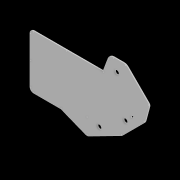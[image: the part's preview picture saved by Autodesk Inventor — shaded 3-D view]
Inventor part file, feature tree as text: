
AUTODESK INVENTOR PART (.ipt)
format: ipt  version: 2020 (Build 240168000, 168)  size: 189,440 bytes
history: native  units: in
note: dims shown in document units (in); Inventor stores cm internally (conversion verified against a paired STEP export)
features: extrude x4, other x4
ambient origin geometry x8: Origin, YZ Plane, XZ Plane, XY Plane, X Axis, Y Axis, Z Axis, Center Point
bodies: Solid1 (feature_tree)
feature tree (8):
  extrude  "BaseFeature"  Depth=0.1in TaperAngle=0.0deg
  extrude  "BatteryMountFeature"  Depth=1.834in
  extrude  "OutputHolesFeature"  Depth=1.49in
  extrude  "USB-CInputFeature"  Depth=1.25in
  other  "Profile"
  other  "BatteryMount"
  other  "Outputs"
  other  "USB-CInput"
